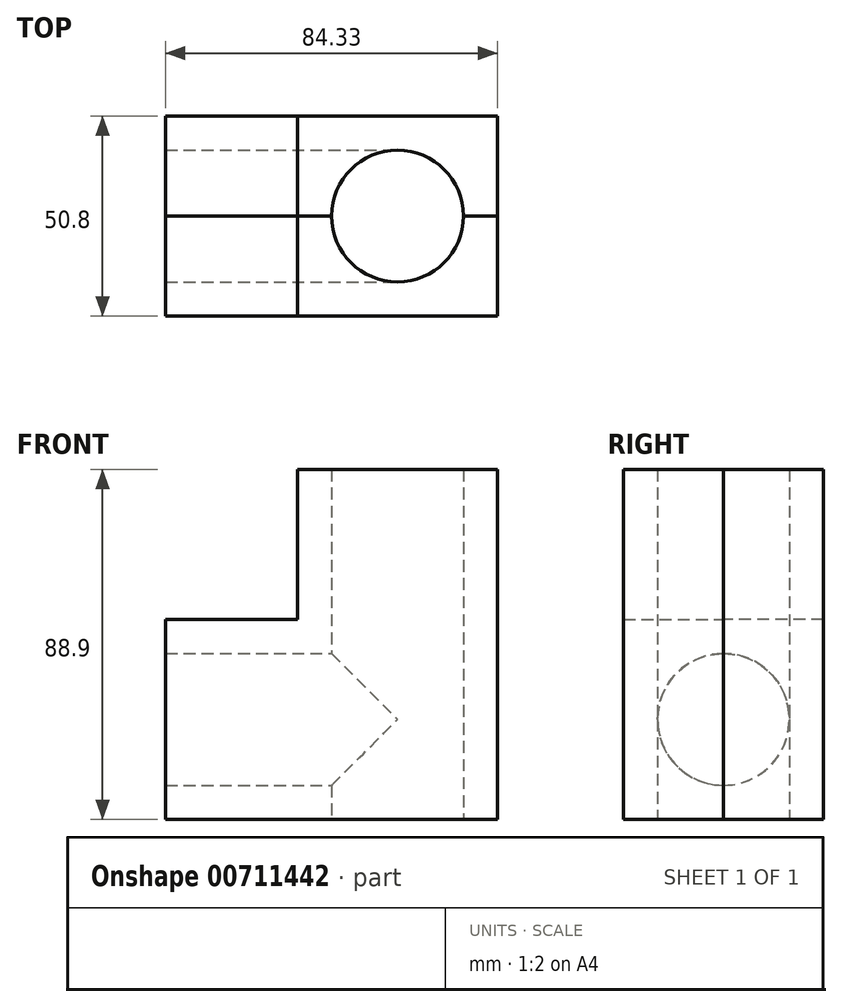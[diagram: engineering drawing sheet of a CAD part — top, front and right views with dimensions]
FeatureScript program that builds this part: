
annotation { "Feature Type Name" : "Feature", "Feature Type Description" : "" }
export const myFeature = defineFeature(function(context is Context, id is Id, definition is map)
    precondition{}
    {
        {
            var Q0;
            Q0=qCreatedBy(makeId("Top.planeOp"),FACE);
            var sketch = newSketch(context, id + "F0", { "sketchPlane" : qUnion([Q0])});
            skCircle(sketch, "E0", {"center": v(0, 0) * mm, "radius": 16.75 * mm});
            skSolve(sketch);
        }
        {
            var Q0;
            Q0=qCreatedBy(makeId("Right.planeOp"),FACE);
            var sketch = newSketch(context, id + "F1", { "sketchPlane" : qUnion([Q0])});
            skCircle(sketch, "E1", {"center": v(0, 31.25) * mm, "radius": 16.75 * mm});
            skLineSegment(sketch, "E2", {"start": v(97, 31.25) * mm, "end": v(-93.8, 31.25) * mm, "construction": true});
            skSolve(sketch);
        }
        {
            var Q0;
            Q0=qCreatedBy(makeId("Front.planeOp"),FACE);
            var sketch = newSketch(context, id + "F2", { "sketchPlane" : qUnion([Q0])});
            skLineSegment(sketch, "E3", {"start": v(-58.93, 56.65) * mm, "end": v(-58.93, 5.85) * mm});
            skLineSegment(sketch, "E4", {"start": v(-58.93, 5.85) * mm, "end": v(25.4, 5.85) * mm});
            skLineSegment(sketch, "E5", {"start": v(25.4, 5.85) * mm, "end": v(25.4, 94.75) * mm});
            skLineSegment(sketch, "E6", {"start": v(25.4, 94.75) * mm, "end": v(-25.4, 94.75) * mm});
            skLineSegment(sketch, "E7", {"start": v(-25.4, 94.75) * mm, "end": v(-25.4, 56.65) * mm});
            skLineSegment(sketch, "E8", {"start": v(-25.4, 56.65) * mm, "end": v(-58.93, 56.65) * mm});
            skLineSegment(sketch, "E9", {"start": v(0, 31.25) * mm, "end": v(-84.56, 31.25) * mm, "construction": true});
            skSolve(sketch);
        }
        {
            var Q0;
            Q0 = qSketchRegion(id + "F2", true);
            extrude(context, id + "F3", {"entities" : qUnion([Q0]), "depth" : 25.4 * mm, "offsetDistance" : 25.4 * mm});
        }
        {
            var Q0;
            Q0 = qSketchRegion(id + "F2", true);
            extrude(context, id + "F4", {"entities" : qUnion([Q0]), "oppositeDirection" : true, "depth" : 25.4 * mm, "offsetDistance" : 25.4 * mm});
        }
        {
            var Q0;
            Q0 = qSketchRegion(id + "F0", true);
            extrude(context, id + "F5", {"entities" : qUnion([Q0]), "operationType" : NewBodyOperationType.REMOVE, "depth" : 152.4 * mm, "offsetDistance" : 25.4 * mm});
        }
        {
            var Q0;
            Q0 = qSketchRegion(id + "F1", true);
            extrude(context, id + "F6", {"entities" : qUnion([Q0]), "operationType" : NewBodyOperationType.REMOVE, "oppositeDirection" : true, "depth" : 157.48 * mm, "offsetDistance" : 25.4 * mm});
        }
    });
